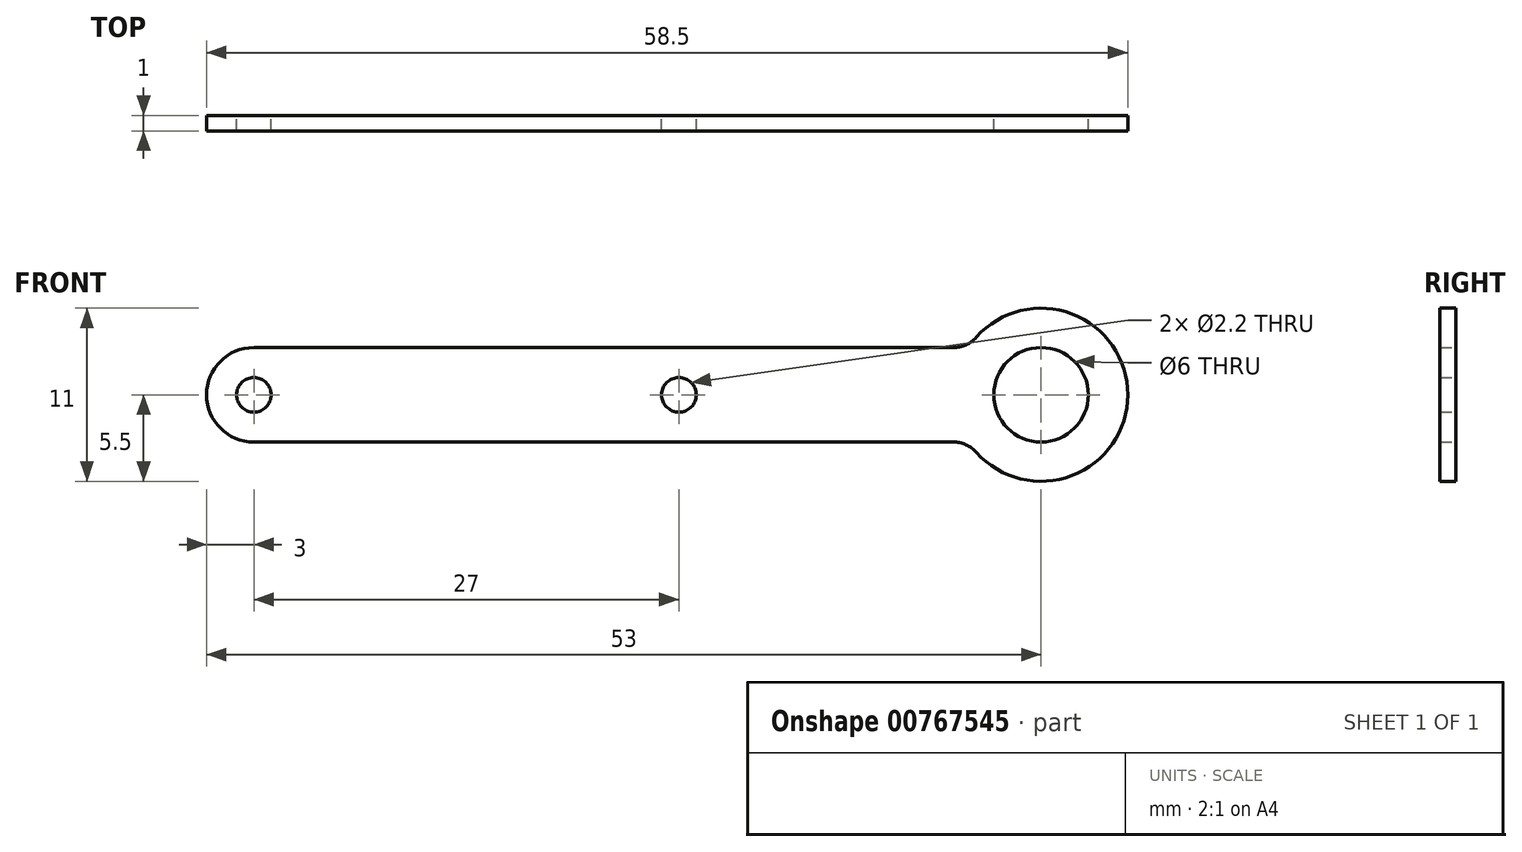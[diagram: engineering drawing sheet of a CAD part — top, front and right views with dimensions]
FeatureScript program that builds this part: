
annotation { "Feature Type Name" : "Feature", "Feature Type Description" : "" }
export const myFeature = defineFeature(function(context is Context, id is Id, definition is map)
    precondition{}
    {
        {
            var Q0;
            Q0=qCreatedBy(makeId("Front.planeOp"),FACE);
            var sketch = newSketch(context, id + "F0", { "sketchPlane" : qUnion([Q0])});
            skArc(sketch, "E0", {"start": v(-4.1, -3.67) * mm, "mid": v(5.5, 0) * mm, "end": v(-4.1, 3.67) * mm});
            skArc(sketch, "E1", {"start": v(-50, 3) * mm, "mid": v(-53, 0) * mm, "end": v(-50, -3) * mm});
            skLineSegment(sketch, "E2", {"start": v(-50, 3) * mm, "end": v(-5.6, 3) * mm});
            skLineSegment(sketch, "E3", {"start": v(-50, -3) * mm, "end": v(-5.6, -3) * mm});
            skPoint(sketch, "E4.visualSharp", {"position": v(-4.6, 3) * mm});
            skArc(sketch, "E4.filletArc", {"start": v(-5.6, 3) * mm, "mid": v(-4.77, 3.17) * mm, "end": v(-4.1, 3.67) * mm});
            skPoint(sketch, "E5.visualSharp", {"position": v(-4.6, -3) * mm});
            skArc(sketch, "E5.filletArc", {"start": v(-4.1, -3.67) * mm, "mid": v(-4.77, -3.17) * mm, "end": v(-5.6, -3) * mm});
            skCircle(sketch, "E6", {"center": v(-50, 0) * mm, "radius": 1.1 * mm});
            skCircle(sketch, "E7", {"center": v(-23, 0) * mm, "radius": 1.1 * mm});
            skCircle(sketch, "E8", {"center": v(0, 0) * mm, "radius": 3 * mm});
            skSolve(sketch);
        }
        {
            var Q0;
            Q0 = qSketchRegion(id + "F0", true);
            extrude(context, id + "F1", {"entities" : qUnion([Q0]), "depth" : 1 * mm, "offsetDistance" : 25 * mm});
        }
    });
